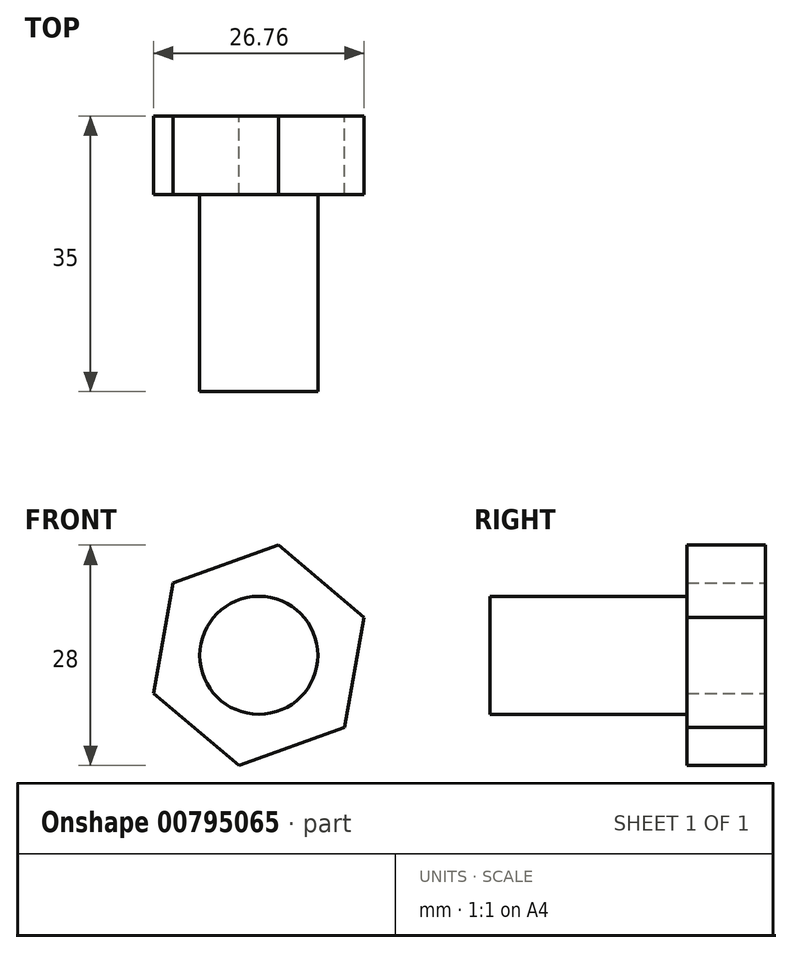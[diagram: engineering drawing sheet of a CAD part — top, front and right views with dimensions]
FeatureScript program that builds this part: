
annotation { "Feature Type Name" : "Feature", "Feature Type Description" : "" }
export const myFeature = defineFeature(function(context is Context, id is Id, definition is map)
    precondition{}
    {
        {
            var Q0;
            Q0=qCreatedBy(makeId("Front.planeOp"),FACE);
            var sketch = newSketch(context, id + "F0", { "sketchPlane" : qUnion([Q0])});
            skCircle(sketch, "E0.cCircle", {"center": v(0, 0) * mm, "radius": 12.32 * mm, "construction": true});
            skLineSegment(sketch, "E0.0", {"start": v(2.51, 14) * mm, "end": v(13.38, 4.83) * mm});
            skLineSegment(sketch, "E0.1", {"start": v(13.38, 4.83) * mm, "end": v(10.87, -9.17) * mm});
            skLineSegment(sketch, "E0.2", {"start": v(10.87, -9.17) * mm, "end": v(-2.51, -14) * mm});
            skLineSegment(sketch, "E0.3", {"start": v(-2.51, -14) * mm, "end": v(-13.38, -4.83) * mm});
            skLineSegment(sketch, "E0.4", {"start": v(-13.38, -4.83) * mm, "end": v(-10.87, 9.17) * mm});
            skLineSegment(sketch, "E0.5", {"start": v(-10.87, 9.17) * mm, "end": v(2.51, 14) * mm});
            skPoint(sketch, "E0.0.midPoint", {"position": v(7.95, 9.41) * mm});
            skCircle(sketch, "E1", {"center": v(0, 0) * mm, "radius": 7.5 * mm});
            skSolve(sketch);
        }
        {
            var Q0;
            Q0=makeQuery(id+"F0.imprint","IMPRINT",FACE,{"disambiguationData":[TD([[makeQuery(id+"F0.imprint","IMPRINT",EDGE,{"derivedFrom":sQuery(id+"F0.wireOp",EDGE,"E1")}),1.0]])]});
            extrude(context, id + "F1", {"entities" : qUnion([Q0]), "depth" : 35 * mm, "offsetDistance" : 25 * mm});
        }
        {
            var Q0;
            Q0=makeQuery(id+"F0.imprint","IMPRINT",FACE,{"disambiguationData":[TD([[makeQuery(id+"F0.imprint","IMPRINT",EDGE,{"derivedFrom":sQuery(id+"F0.wireOp",EDGE,"E0.0")}),-1.0]])]});
            extrude(context, id + "F2", {"entities" : qUnion([Q0]), "operationType" : NewBodyOperationType.ADD, "depth" : 10 * mm, "offsetDistance" : 25 * mm});
        }
    });
